# Revit family: КСБ ЕС_Eng
name_source: partatom
category: Mechanical Equipment
units: mm (PartAtom-declared; Revit-internal decimal feet)

## family parameters
Always vertical = Yes
Classification = None
Cut with Voids When Loaded = No
Part Type = Normal
Room Calculation Point = No
Round Connector Dimension = Use Diameter
Shared = No
Work Plane-Based = No

## types (7) — shared parameters
00_20_Manufacturer = Vents
00_20_Name = Sound-insulated fan with EC motor
Amperage = 1 A
Casing Material = Steel, galvanized
Frequency = 50 Hz
Load Classification = HVAC
Maintenance zone material = <By Category>
Manufacturer = Vents
Number of Fase = 1
URL = https://ventilation-system.com
Voltage = 230 V
zero-valued in all types: Default Elevation

## per-type parameters (varying)
| type | B | B1 | B2 | B3 | D1 | Diameter | Dy | H | Height | L | L2 | Length | Maximum Air Flow | Power | Weight | Width | h | h1 | l |
| KSB 100 EC | 355 mm | 447 mm | 380 mm  [stored 1.24672 ft] | 89 mm | 102 mm | 100 mm  [stored 0.328084 ft] | 100 mm  [stored 0.328084 ft] | 200 mm  [stored 0.656168 ft] | 200 mm  [stored 0.656168 ft] | 325 mm  [stored 1.06627 ft] | 280 mm  [stored 0.918635 ft] | 447 mm | 77.0 L/s | 93 W | 5.40 kg | 375 mm  [stored 1.23031 ft] | 100 mm  [stored 0.328084 ft] | 150 mm | 46 mm  [stored 0.150919 ft] |
| KSB 315 EC | 545 mm | 650 mm | 566 mm | 136 mm | 317 mm  [stored 1.04003 ft] | 315 mm  [stored 1.03346 ft] | 315 mm  [stored 1.03346 ft] | 405 mm | 405 mm | 435 mm | 438 mm | 650 mm | 350.0 L/s | 164 W | 15.50 kg | 485 mm | 203 mm | 304 mm | 53 mm |
| KSB 125 EC | 355 mm | 447 mm | 380 mm  [stored 1.24672 ft] | 89 mm | 127 mm | 125 mm  [stored 0.410105 ft] | 125 mm  [stored 0.410105 ft] | 200 mm  [stored 0.656168 ft] | 200 mm  [stored 0.656168 ft] | 325 mm  [stored 1.06627 ft] | 280 mm  [stored 0.918635 ft] | 447 mm | 99.0 L/s | 93 W | 5.40 kg | 375 mm  [stored 1.23031 ft] | 100 mm  [stored 0.328084 ft] | 150 mm | 46 mm  [stored 0.150919 ft] |
| KSB 160 EC | 385 mm  [stored 1.26312 ft] | 477 mm | 410 mm  [stored 1.34514 ft] | 96 mm | 162 mm  [stored 0.531496 ft] | 160 mm  [stored 0.524934 ft] | 160 mm  [stored 0.524934 ft] | 220 mm  [stored 0.721785 ft] | 220 mm  [stored 0.721785 ft] | 355 mm | 310 mm  [stored 1.01706 ft] | 477 mm | 118.0 L/s | 95 W | 6.40 kg | 405 mm | 110 mm  [stored 0.360892 ft] | 165 mm | 46 mm  [stored 0.150919 ft] |
| KSB 200 EC | 485 mm | 590 mm | 506 mm | 121 mm | 202 mm  [stored 0.66273 ft] | 200 mm  [stored 0.656168 ft] | 200 mm  [stored 0.656168 ft] | 295 mm  [stored 0.967848 ft] | 295 mm  [stored 0.967848 ft] | 435 mm | 368 mm  [stored 1.20735 ft] | 590 mm | 194.0 L/s | 102 W | 10.00 kg | 485 mm | 148 mm | 221 mm | 53 mm |
| KSB 250 EC | 485 mm | 590 mm | 506 mm | 121 mm | 252 mm  [stored 0.826772 ft] | 250 mm  [stored 0.82021 ft] | 250 mm  [stored 0.82021 ft] | 295 mm  [stored 0.967848 ft] | 295 mm  [stored 0.967848 ft] | 435 mm | 368 mm  [stored 1.20735 ft] | 590 mm | 318.0 L/s | 164 W | 12.50 kg | 485 mm | 148 mm | 221 mm | 53 mm |
| KSB 150 EC | 385 mm  [stored 1.26312 ft] | 447 mm | 410 mm  [stored 1.34514 ft] | 96 mm | 152 mm  [stored 0.498688 ft] | 150 mm | 150 mm | 220 mm  [stored 0.721785 ft] | 220 mm  [stored 0.721785 ft] | 325 mm  [stored 1.06627 ft] | 310 mm  [stored 1.01706 ft] | 447 mm | 118.0 L/s | 95 W | 6.40 kg | 375 mm  [stored 1.23031 ft] | 110 mm  [stored 0.360892 ft] | 165 mm | 31 mm  [stored 0.101706 ft] |

note: column(s) folded — value = type name in every type: 00_20_Type

note: [stored X ft] marks values corroborated as IEEE doubles in the binary element streams (Revit-internal decimal feet)
